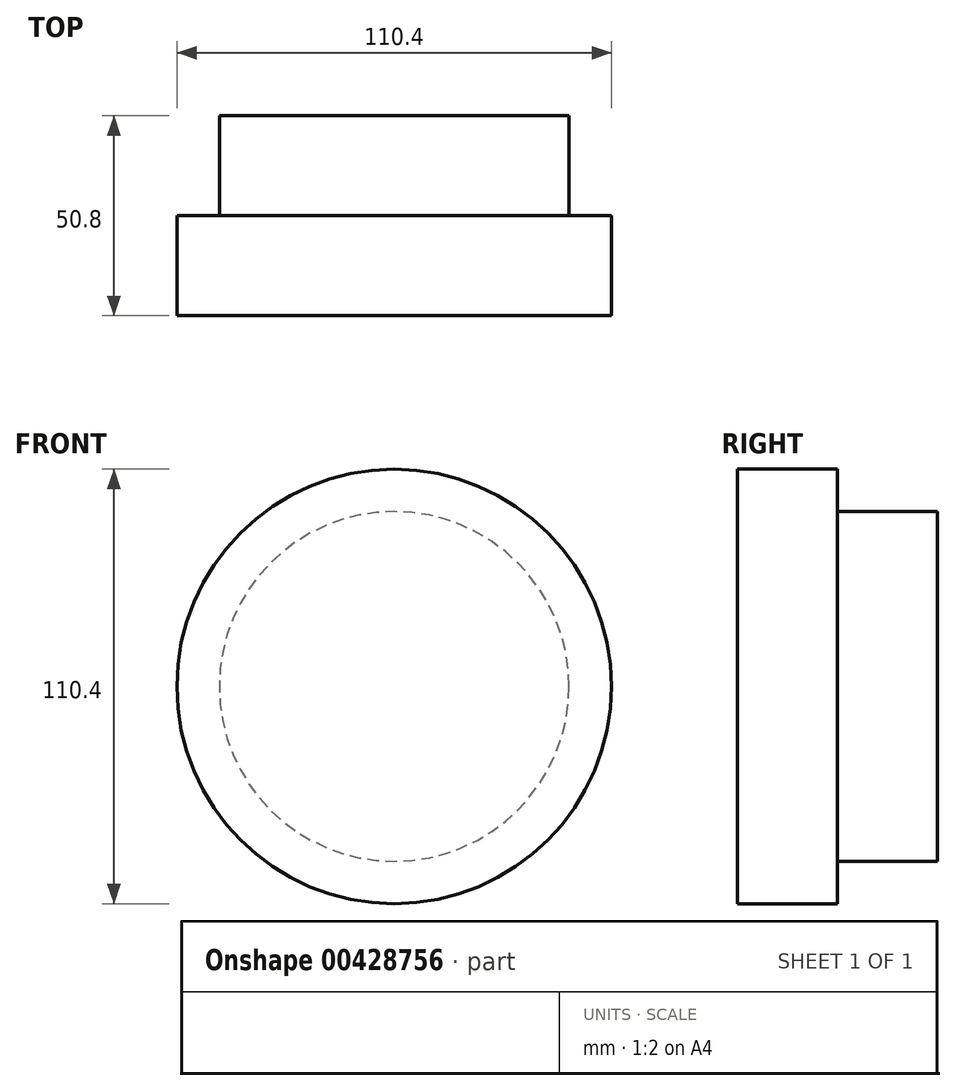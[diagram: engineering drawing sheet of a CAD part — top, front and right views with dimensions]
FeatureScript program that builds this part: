
annotation { "Feature Type Name" : "Feature", "Feature Type Description" : "" }
export const myFeature = defineFeature(function(context is Context, id is Id, definition is map)
    precondition{}
    {
        {
            var Q0;
            Q0=qCreatedBy(makeId("Front.planeOp"),FACE);
            var sketch = newSketch(context, id + "F0", { "sketchPlane" : qUnion([Q0])});
            skCircle(sketch, "E0", {"center": v(0, 0) * mm, "radius": 55.2 * mm});
            skSolve(sketch);
        }
        {
            var Q0;
            Q0 = qSketchRegion(id + "F0", true);
            extrude(context, id + "F1", {"entities" : qUnion([Q0]), "depth" : 25.4 * mm});
        }
        {
            var Q0;
            Q0=qCreatedBy(makeId("Front.planeOp"),FACE);
            var sketch = newSketch(context, id + "F2", { "sketchPlane" : qUnion([Q0])});
            skCircle(sketch, "E1.0", {"center": v(0, 0) * mm, "radius": 44.42 * mm});
            skSolve(sketch);
        }
        {
            var Q0;
            Q0 = qSketchRegion(id + "F2", true);
            var sketch = newSketch(context, id + "F3", { "sketchPlane" : qUnion([Q0])});
            skSolve(sketch);
        }
        {
            var Q0;
            Q0=makeQuery(id+"F2.imprint","IMPRINT",FACE,{"disambiguationData":[TD([[makeQuery(id+"F2.imprint","IMPRINT",EDGE,{"derivedFrom":sQuery(id+"F2.wireOp",EDGE,"E1.0")}),1.0]])]});
            extrude(context, id + "F4", {"entities" : qUnion([Q0]), "operationType" : NewBodyOperationType.ADD, "depth" : 25.4 * mm});
        }
        {
            var Q0;
            Q0=makeQuery(id+"F3.imprint","IMPRINT",FACE,{"disambiguationData":[TD([[makeQuery(id+"F3.imprint","IMPRINT",EDGE,{"derivedFrom":makeQuery(id+"F2.imprint","IMPRINT",EDGE,{"derivedFrom":sQuery(id+"F2.wireOp",EDGE,"E1.0")})}),1.0]])]});
            extrude(context, id + "F5", {"entities" : qUnion([Q0]), "operationType" : NewBodyOperationType.ADD, "oppositeDirection" : true, "depth" : 25.4 * mm});
        }
        {
            var Q0;
            Q0=makeQuery(id+"F5.opExtrude","CAP_FACE",FACE,{"disambiguationData":[OSD([sQuery(id+"F2.wireOp",EDGE,"E1.0")])],"isStart":false});
            var sketch = newSketch(context, id + "F6", { "sketchPlane" : qUnion([Q0])});
            skCircle(sketch, "E2.0", {"center": v(0, 0) * mm, "radius": 50.77 * mm});
            skCircle(sketch, "E3.0", {"center": v(0, 0) * mm, "radius": 35.18 * mm});
            skSolve(sketch);
        }
        {
            var Q0;
            Q0=makeQuery(id+"F6.imprint","IMPRINT",FACE,{"disambiguationData":[TD([[makeQuery(id+"F6.imprint","IMPRINT",EDGE,{"derivedFrom":sQuery(id+"F6.wireOp",EDGE,"E3.0")}),1.0]])]});
            var sketch = newSketch(context, id + "F7", { "sketchPlane" : qUnion([Q0])});
            skSolve(sketch);
        }
        {
            var Q0;
            Q0=makeQuery(id+"F6.imprint","IMPRINT",FACE,{"disambiguationData":[TD([[makeQuery(id+"F6.imprint","IMPRINT",EDGE,{"derivedFrom":sQuery(id+"F6.wireOp",EDGE,"E3.0")}),1.0]])]});
            extrude(context, id + "F8", {"entities" : qUnion([Q0]), "operationType" : NewBodyOperationType.ADD, "oppositeDirection" : true, "depth" : 50.8 * mm});
        }
    });
